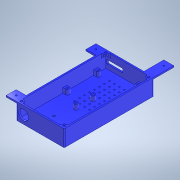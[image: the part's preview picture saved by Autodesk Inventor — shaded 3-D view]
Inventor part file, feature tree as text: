
AUTODESK INVENTOR PART (.ipt)
format: ipt  version: 2022 (Build 260153000, 153)  size: 417,280 bytes
history: native  units: in
note: dims shown in document units (in); Inventor stores cm internally (conversion verified against a paired STEP export)
features: reference x15, extrude x12, sketch x12, projected_geometry x5, other x5, plane x3, mirror x2, pattern_linear x1, hole x1, chamfer x1, fillet x1
ambient origin geometry x8: Origin, YZ Plane, XZ Plane, XY Plane, X Axis, Y Axis, Z Axis, Center Point
bodies: Body1 (feature_tree)
feature tree (58):
  plane  "Work Plane2"
  extrude  "Extrusion14"  Depth=0.7874in
  extrude  "Extrusion15"  Depth=0.1181in TaperAngle=0.0deg
  extrude  "Extrusion17"  Depth=1.1811in TaperAngle=0.0deg
  extrude  "Extrusion18"  Depth=0.1575in
  extrude  "Extrusion19"  Depth=0.3937in TaperAngle=0.0deg
  pattern_linear  "Rectangular Pattern1"  Count1=8 Spacing1=0.3937in
  extrude  "Extrusion20"  Depth=0.3937in
  extrude  "Extrusion21"  Depth=0.3937in TaperAngle=0.0deg
  extrude  "Extrusion22"  Depth=0.0787in
  extrude  "Extrusion23"  Depth=0.0787in
  hole  "Hole19"  [1 undecoded]
  sketch  "Sketch32"  dims[d136=1.9685in d138=0.3937in d139=0.5906in]
  extrude  "Extrusion24"  Depth=0.0787in
  extrude  "Extrusion25"  Depth=0.3937in TaperAngle=0.0deg
  plane  "Work Plane3"
  plane  "Work Plane4"
  mirror  "Mirror1"
  mirror  "Mirror2"
  chamfer  "Chamfer2"  Distance=0.3937in
  fillet  "Fillet2"  Radius=1.5748in
  extrude  "Extrusion26"  Depth=0.1181in TaperAngle=0.0deg
  sketch  "Sketch22"  dims[d108=0.2756in d109=0.7874in]
  reference  "Reference1"
  reference  "Reference2"
  reference  "Reference3"
  sketch  "Sketch23"  dims[d111=0.7874in d112=0.1181in d113=0.0in]
  projected_geometry  "Projected Loop2"
  sketch  "Sketch24"  dims[d114=0.1181in d115=1.1811in d116=0.0in]
  reference  "Reference4"
  reference  "Reference5"
  reference  "Reference6"
  reference  "Reference7"
  reference  "Reference8"
  sketch  "Sketch25"  dims[d117=0.1969in d122=0.1575in]
  projected_geometry  "Projected Loop3"
  sketch  "Sketch26"  dims[d123=0.315in d124=0.3937in d125=0.0in]
  sketch  "Sketch27"  dims[d126=0.1575in d127=0.0in]
  projected_geometry  "Projected Loop4"
  sketch  "Sketch28"  dims[d128=0.1181in]
  reference  "Reference9"
  reference  "Reference10"
  reference  "Reference11"
  reference  "Reference12"
  reference  "Reference13"
  sketch  "Sketch29"  dims[d129=0.7283in]
  projected_geometry  "Projected Loop5"
  sketch  "Sketch30"  dims[d130=0.9843in]
  sketch  "Sketch31"  dims[d131=0.3937in d132=0.0in d133=3.1496in d135=0.3937in]
  projected_geometry  "Projected Loop6"
  sketch  "Sketch33"  dims[d140=0.7874in d141=0.3937in d142=0.0in d143=0.0787in d144=0.0787in d145=0.0787in d146=0.0787in d147=0.3937in d148=0.0in d149=0.3937in d150=0.0in d151=1.5748in d152=0.1181in d153=0.0in d154=0.126in d155=0.2362in d156=0.119in d157=0.0787in d158=0.563in d159=0.315in d160=0.8108in d161=0.1969in d162=0.0787in d163=0.0787in d164=0.0in d165=0.0689in d166=0.0in d170=0.2236in d171=0.0787in d172=45.0deg d173=0.0787in d174=0.7874in d175=0.0in d176=0.0in]
  reference  "Reference14"
  reference  "Reference15"
  parser-record x1  (decoder bookkeeping rows leaked as tree rows — omitted from the tree; the rows remain in map.json)
  other  "Electronics Box.iam"
  other  "SKR MINI E3 V1.2:1"
  other  "SSR-40:1"
  other  "SKR Mini E3 v2.0:1"
note: 1 required parameter value undecoded (feature->parameter linkage not recoverable at this tier; creation-order binding heuristic only, values carry confidence <= 0.55)
note: 1 file-system path scrubbed to <path> (originals preserved in map.json)
